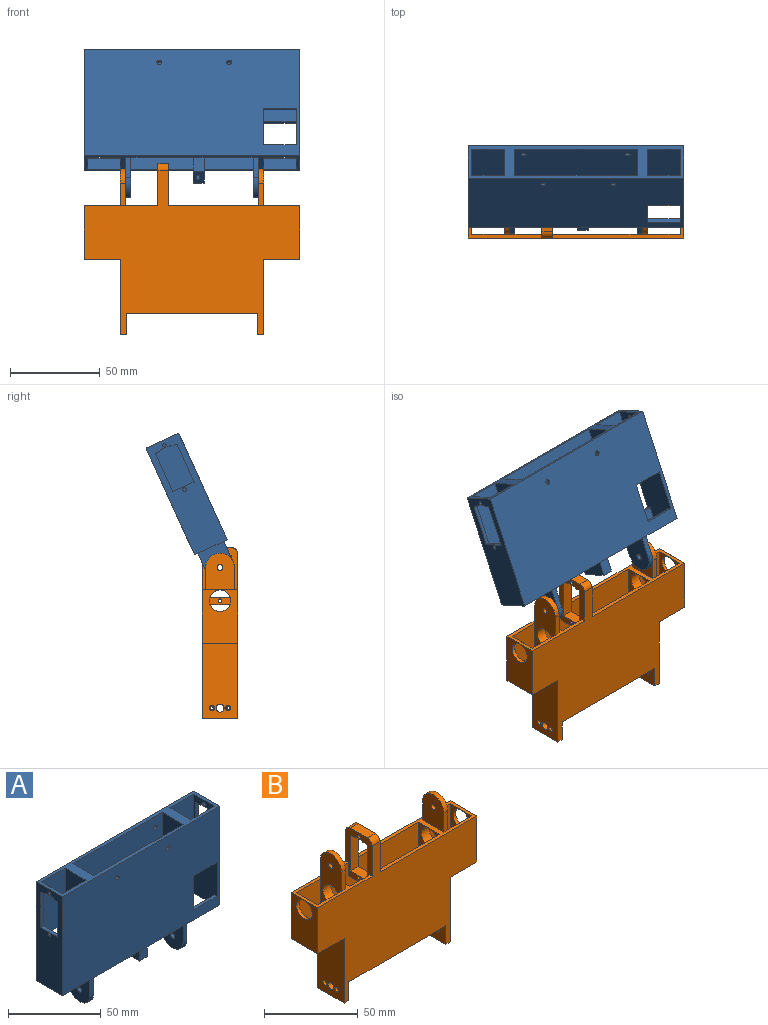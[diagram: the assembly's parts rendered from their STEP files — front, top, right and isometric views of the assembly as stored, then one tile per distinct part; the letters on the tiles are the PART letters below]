
ASSEMBLY  parts=2 mates=1
PART A: 78 faces, bbox 120x20x85.7 mm
  f0: plane 18x6.8mm, normal (0,1,0), area 122.5mm2, adj f17,f24,f33,f75
  f1: plane 18x6.8mm, normal (0,-1,0), area 122.5mm2, adj f17,f24,f33,f73
  f2: plane 18x6.8mm, normal (0,-1,0), area 122.5mm2, adj f27,f30,f33,f71
  f3: plane 120x65.32mm, normal (0,1,0), area 7010.2mm2, adj f16,f17,f21,f24,f27,f30,f32,f33
  f4: plane 13x2mm, normal (0,0,1), area 26mm2, adj f11,f15,f21,f30
  f5: plane 2.8x2mm, normal (0,0,-1), area 5.6mm2, adj f7,f14,f21,f30
  f6: plane 2x0.7mm, normal (0,1,0), area 1.4mm2, adj f8,f13,f21,f30
  f7: plane 2x0.7mm, normal (0,-1,0), area 1.4mm2, adj f5,f8,f21,f30
  f8: plane 6x2mm, normal (0,0,-1), area 12mm2, adj f6,f7,f21,f30
  f9: cylinder r=1mm len=2mm, axis (-1,0,0), area 12.6mm2, adj f21,f30
  f10: cylinder r=1mm len=2mm, axis (-1,0,0), area 12.6mm2, adj f21,f30
  f11: plane 22.8x2mm, normal (0,-1,0), area 45.6mm2, adj f4,f14,f21,f30
  f12: cylinder r=0.7mm len=2mm, axis (-1,0,0), area 2.2mm2, adj f13,f15,f21,f30
  f13: plane 2.8x2mm, normal (0,0,-1), area 5.6mm2, adj f6,f12,f21,f30
  f14: cylinder r=0.7mm len=2mm, axis (1,0,0), area 2.2mm2, adj f5,f11,f21,f30
  f15: plane 22.8x2mm, normal (0,1,0), area 45.6mm2, adj f4,f12,f21,f30
  f16: plane 65.32x20mm, normal (1,0,0), area 990.7mm2, adj f3,f18,f22,f32,f33,f55,f56,f57
  f17: plane 65.32x20mm, normal (-1,0,0), area 818.9mm2, adj f0,f1,f3,f18,f22,f23,f25,f32
  f18: plane 2.8x2mm, normal (0,0,-1), area 5.6mm2, adj f16,f17,f58,f67
  f19: plane 68x65.32mm, normal (0,-1,0), area 4360.7mm2, adj f29,f31,f32,f33,f46,f47,f49,f62
  f20: plane 68x65.32mm, normal (0,1,0), area 4372.6mm2, adj f29,f31,f32,f33,f46,f47,f49,f76
  f21: plane 65.32x20mm, normal (-1,0,0), area 990.7mm2, adj f3,f4,f5,f6,f7,f8,f9,f10
  f22: plane 120x65.32mm, normal (0,-1,0), area 7424.6mm2, adj f16,f17,f21,f24,f32,f33,f74,f75
  f23: plane 36.16x18mm, normal (0,1,0), area 650.9mm2, adj f17,f24,f32,f74
  f24: plane 65.32x20mm, normal (1,0,0), area 1134.6mm2, adj f0,f1,f3,f22,f23,f25,f32,f33
  f25: plane 36.16x18mm, normal (0,-1,0), area 650.9mm2, adj f17,f24,f32,f72
  f26: plane 36.16x18mm, normal (0,-1,0), area 650.9mm2, adj f27,f30,f32,f70
  f27: plane 65.32x18mm, normal (-1,0,0), area 1089.9mm2, adj f2,f3,f26,f28,f32,f33,f70,f71
  f28: plane 65.32x18mm, normal (0,1,0), area 1175.8mm2, adj f27,f30,f32,f33
  f29: plane 85.66x16mm, normal (1,0,0), area 1335.1mm2, adj f19,f20,f32,f37,f41,f42,f43
  f30: plane 65.32x18mm, normal (1,0,0), area 774.1mm2, adj f2,f3,f4,f5,f6,f7,f8,f9
  f31: plane 85.66x16mm, normal (-1,0,0), area 1335.1mm2, adj f19,f20,f32,f36,f38,f39,f40
  f32: plane 120x20mm, normal (0,0,1), area 736mm2, adj f3,f16,f17,f19,f20,f21,f22,f23
  f33: plane 120x20mm, normal (0,0,-1), area 640mm2, adj f0,f1,f2,f3,f16,f17,f19,f20
  f34: plane 20.34x16mm, normal (-1,0,0), area 289.9mm2, adj f33,f37,f41,f42,f43
  f35: plane 20.34x16mm, normal (1,0,0), area 289.9mm2, adj f33,f36,f38,f39,f40
  f36: cylinder r=1.6mm len=3.2mm, axis (1,0,0), area 30.2mm2, adj f31,f35
  f37: cylinder r=1.6mm len=3.2mm, axis (1,0,0), area 30.2mm2, adj f29,f34
  f38: plane 12.34x3mm, normal (0,1,0), area 37mm2, adj f31,f33,f35,f39
  f39: cylinder r=8mm len=16mm, axis (1,0,0), area 75.4mm2, adj f31,f35,f38,f40
  f40: plane 12.34x3mm, normal (0,-1,0), area 37mm2, adj f31,f33,f35,f39
  f41: plane 12.34x3mm, normal (0,-1,0), area 37mm2, adj f29,f33,f34,f42
  f42: cylinder r=8mm len=16mm, axis (1,0,0), area 75.4mm2, adj f29,f34,f41,f43
  f43: plane 12.34x3mm, normal (0,1,0), area 37mm2, adj f29,f33,f34,f42
  f44: plane 8.54x6mm, normal (0,1,0), area 51.2mm2, adj f33,f45,f46,f47
  f45: plane 16x6mm, normal (0,0,-1), area 85.2mm2, adj f44,f46,f47,f48,f50,f51,f52,f53
  f46: plane 18.14x16mm, normal (-1,0,0), area 290.3mm2, adj f19,f20,f44,f45,f48,f49
  f47: plane 18.14x16mm, normal (1,0,0), area 290.3mm2, adj f19,f20,f44,f45,f48,f49
  f48: plane 8.54x6mm, normal (0,-1,0), area 51.2mm2, adj f33,f45,f46,f47
  f49: plane 16x6mm, normal (0,0,1), area 96mm2, adj f19,f20,f46,f47
  f50: plane 12.4x5.69mm, normal (1,0,0), area 59.1mm2, adj f45,f51,f52,f54
  f51: plane 10.21x1.9mm, normal (0,1,-0.06), area 19.4mm2, adj f45,f50,f53,f54
  f52: plane 10.21x1.9mm, normal (0,-1,-0.06), area 19.4mm2, adj f45,f50,f53,f54
  f53: plane 12.4x5.69mm, normal (-1,0,0), area 59.1mm2, adj f45,f51,f52,f54
  f54: cylinder r=2.2mm len=4.4mm, axis (1,0,0), area 13.1mm2, adj f50,f51,f52,f53
  f55: plane 2.8x2mm, normal (0,0,-1), area 5.6mm2, adj f16,f17,f59,f66
  f56: plane 22.8x2mm, normal (0,-1,0), area 45.6mm2, adj f16,f17,f58,f69
  f57: plane 22.8x2mm, normal (0,1,0), area 45.6mm2, adj f16,f17,f59,f69
  f58: cylinder r=0.7mm len=2mm, axis (-1,0,0), area 2.2mm2, adj f16,f17,f18,f56
  f59: cylinder r=0.7mm len=2mm, axis (1,0,0), area 2.2mm2, adj f16,f17,f55,f57
  f60: cylinder r=1mm len=2mm, axis (1,0,0), area 12.6mm2, adj f16,f17
  f61: cylinder r=1mm len=2mm, axis (1,0,0), area 12.6mm2, adj f16,f17
  f62: cylinder r=1.38mm len=2.75mm, axis (0,1,0), area 17.3mm2, adj f3,f19
  f63: cylinder r=1.38mm len=2.75mm, axis (0,1,0), area 17.3mm2, adj f3,f19
  f64: cylinder r=1.38mm len=2.75mm, axis (0,1,0), area 17.3mm2, adj f3,f19
  f65: cylinder r=1.38mm len=2.75mm, axis (0,1,0), area 17.3mm2, adj f3,f19
  f66: plane 2x0.7mm, normal (0,1,0), area 1.4mm2, adj f16,f17,f55,f68
  f67: plane 2x0.7mm, normal (0,-1,0), area 1.4mm2, adj f16,f17,f18,f68
  f68: plane 6x2mm, normal (0,0,-1), area 12mm2, adj f16,f17,f66,f67
  f69: plane 13x2mm, normal (0,0,1), area 26mm2, adj f16,f17,f56,f57
  f70: plane 18x2mm, normal (0,0,-1), area 36mm2, adj f3,f26,f27,f30
  f71: plane 18x2mm, normal (0,0,1), area 36mm2, adj f2,f3,f27,f30
  f72: plane 18x2mm, normal (0,0,-1), area 36mm2, adj f3,f17,f24,f25
  f73: plane 18x2mm, normal (0,0,1), area 36mm2, adj f1,f3,f17,f24
  f74: plane 18x2mm, normal (0,0,-1), area 36mm2, adj f17,f22,f23,f24
  f75: plane 18x2mm, normal (0,0,1), area 36mm2, adj f0,f17,f22,f24
  f76: cylinder r=1.38mm len=2.75mm, axis (0,-1,0), area 17.3mm2, adj f20,f22
  f77: cylinder r=1.38mm len=2.75mm, axis (0,-1,0), area 17.3mm2, adj f20,f22
PART B: 75 faces, bbox 120x20x95.3 mm
  f0: plane 120x91.75mm, normal (0,1,0), area 6190mm2, adj f2,f4,f7,f8,f14,f15,f18,f19
  f1: plane 68x60mm, normal (0,-1,0), area 4016.7mm2, adj f2,f4,f7,f8,f14,f27,f28,f47
  f2: plane 31.8x20mm, normal (1,0,0), area 280.9mm2, adj f0,f1,f3,f5,f6,f7,f9,f47
  f3: plane 6x2.8mm, normal (0,0,-1), area 16.8mm2, adj f2,f4,f51,f67
  f4: plane 31.8x20mm, normal (-1,0,0), area 280.9mm2, adj f0,f1,f3,f5,f6,f8,f9,f47
  f5: plane 120x91.75mm, normal (0,-1,0), area 6202.5mm2, adj f2,f4,f7,f8,f14,f15,f18,f19
  f6: plane 12.83x6mm, normal (0,0,1), area 77mm2, adj f2,f4,f65,f66
  f7: plane 73x20mm, normal (0,0,1), area 372mm2, adj f0,f1,f2,f5,f9,f17,f24,f28
  f8: plane 41x20mm, normal (0,0,1), area 244mm2, adj f0,f1,f4,f5,f9,f16,f20,f27
  f9: plane 68x60mm, normal (0,1,0), area 4029.2mm2, adj f2,f4,f7,f8,f14,f27,f28,f47
  f10: cylinder r=0.8mm len=1.9mm, axis (-1,0,0), area 9.6mm2, adj f55,f64
  f11: cylinder r=0.8mm len=1.9mm, axis (-1,0,0), area 9.6mm2, adj f55,f62
  f12: cylinder r=0.8mm len=1.9mm, axis (-1,0,0), area 9.6mm2, adj f56,f60
  f13: cylinder r=0.8mm len=1.9mm, axis (-1,0,0), area 9.6mm2, adj f56,f58
  f14: plane 73x20mm, normal (0,0,-1), area 372mm2, adj f0,f1,f5,f9,f27,f28,f55,f56
  f15: plane 92.34x20mm, normal (-1,0,0), area 1466.8mm2, adj f0,f5,f21,f22,f25,f32,f34,f36
  f16: plane 20.34x16mm, normal (1,0,0), area 289.9mm2, adj f8,f36,f40,f41,f42
  f17: plane 20.34x16mm, normal (-1,0,0), area 289.9mm2, adj f7,f35,f37,f38,f39
  f18: plane 20x20mm, normal (0,0,-1), area 112mm2, adj f0,f5,f23,f24,f29,f30,f31
  f19: plane 20x3.5mm, normal (0,0,-1), area 70mm2, adj f0,f5,f23,f56
  f20: plane 30x20mm, normal (-1,0,0), area 486.9mm2, adj f0,f5,f8,f21,f45
  f21: plane 20x20mm, normal (0,0,-1), area 112mm2, adj f0,f5,f15,f20,f32,f33,f34
  f22: plane 20x3.5mm, normal (0,0,-1), area 70mm2, adj f0,f5,f15,f55
  f23: plane 92.34x20mm, normal (1,0,0), area 1466.8mm2, adj f0,f5,f18,f19,f26,f29,f31,f35
  f24: plane 30x20mm, normal (1,0,0), area 486.9mm2, adj f0,f5,f7,f18,f43
  f25: cylinder r=2.25mm len=4.5mm, axis (-1,0,0), area 49.5mm2, adj f15,f55
  f26: cylinder r=2.25mm len=4.5mm, axis (-1,0,0), area 49.5mm2, adj f23,f56
  f27: plane 60x16mm, normal (1,0,0), area 846.9mm2, adj f1,f8,f9,f14,f46
  f28: plane 60x16mm, normal (-1,0,0), area 846.9mm2, adj f1,f7,f9,f14,f44
  f29: plane 30x18mm, normal (0,-1,0), area 540mm2, adj f7,f18,f23,f30
  f30: plane 30x16mm, normal (-1,0,0), area 366.9mm2, adj f7,f18,f29,f31,f43
  f31: plane 30x18mm, normal (0,1,0), area 540mm2, adj f7,f18,f23,f30
  f32: plane 30x18mm, normal (0,1,0), area 540mm2, adj f8,f15,f21,f33
  f33: plane 30x16mm, normal (1,0,0), area 366.9mm2, adj f8,f21,f32,f34,f45
  f34: plane 30x18mm, normal (0,-1,0), area 540mm2, adj f8,f15,f21,f33
  f35: cylinder r=1.6mm len=3.2mm, axis (1,0,0), area 30.2mm2, adj f17,f23
  f36: cylinder r=1.6mm len=3.2mm, axis (1,0,0), area 30.2mm2, adj f15,f16
  f37: plane 12.34x3mm, normal (0,-1,0), area 37mm2, adj f7,f17,f23,f39
  f38: plane 12.34x3mm, normal (0,1,0), area 37mm2, adj f7,f17,f23,f39
  f39: cylinder r=8mm len=16mm, axis (1,0,0), area 75.4mm2, adj f17,f23,f37,f38
  f40: cylinder r=8mm len=16mm, axis (1,0,0), area 75.4mm2, adj f15,f16,f41,f42
  f41: plane 12.34x3mm, normal (0,1,0), area 37mm2, adj f8,f15,f16,f40
  f42: plane 12.34x3mm, normal (0,-1,0), area 37mm2, adj f8,f15,f16,f40
  f43: cylinder r=6mm len=12mm, axis (-1,0,0), area 75.4mm2, adj f24,f30
  f44: cylinder r=6mm len=12mm, axis (-1,0,0), area 226.2mm2, adj f23,f28
  f45: cylinder r=6mm len=12mm, axis (1,0,0), area 75.4mm2, adj f20,f33
  f46: cylinder r=6mm len=12mm, axis (1,0,0), area 226.2mm2, adj f15,f27
  f47: plane 16x6mm, normal (0,0,-1), area 96mm2, adj f1,f2,f4,f9
  f48: cylinder r=1mm len=6mm, axis (1,0,0), area 37.7mm2, adj f2,f4
  f49: plane 22.8x6mm, normal (0,-1,0), area 136.8mm2, adj f2,f4,f51,f70
  f50: plane 22.8x6mm, normal (0,1,0), area 136.8mm2, adj f2,f4,f52,f70
  f51: cylinder r=0.7mm len=6mm, axis (-1,0,0), area 6.6mm2, adj f2,f3,f4,f49
  f52: cylinder r=0.7mm len=6mm, axis (1,0,0), area 6.6mm2, adj f2,f4,f50,f53
  f53: plane 6x2.8mm, normal (0,0,-1), area 16.8mm2, adj f2,f4,f52,f68
  f54: cylinder r=1mm len=6mm, axis (1,0,0), area 37.7mm2, adj f2,f4
  f55: plane 20x12mm, normal (1,0,0), area 220.1mm2, adj f0,f5,f10,f11,f14,f22,f25
  f56: plane 20x12mm, normal (-1,0,0), area 220.1mm2, adj f0,f5,f12,f13,f14,f19,f26
  f57: cylinder r=1.5mm len=3mm, axis (1,0,0), area 15.1mm2, adj f23,f58
  f58: plane 3x3mm, normal (1,0,0), area 5.1mm2, adj f13,f57
  f59: cylinder r=1.5mm len=3mm, axis (1,0,0), area 15.1mm2, adj f23,f60
  f60: plane 3x3mm, normal (1,0,0), area 5.1mm2, adj f12,f59
  f61: cylinder r=1.5mm len=3mm, axis (-1,0,0), area 15.1mm2, adj f15,f62
  f62: plane 3x3mm, normal (-1,0,0), area 5.1mm2, adj f11,f61
  f63: cylinder r=1.5mm len=3mm, axis (-1,0,0), area 15.1mm2, adj f15,f64
  f64: plane 3x3mm, normal (-1,0,0), area 5.1mm2, adj f10,f63
  f65: cylinder r=3.58mm len=6mm, axis (-1,0,0), area 33.8mm2, adj f2,f4,f5,f6
  f66: cylinder r=3.58mm len=6mm, axis (-1,0,0), area 33.8mm2, adj f0,f2,f4,f6
  f67: plane 6x0.7mm, normal (0,-1,0), area 4.2mm2, adj f2,f3,f4,f69
  f68: plane 6x0.7mm, normal (0,1,0), area 4.2mm2, adj f2,f4,f53,f69
  f69: plane 6x6mm, normal (0,0,-1), area 36mm2, adj f2,f4,f67,f68
  f70: plane 13x6mm, normal (0,0,1), area 78mm2, adj f2,f4,f49,f50
  f71: cylinder r=1mm len=2mm, axis (0,1,0), area 12.6mm2, adj f0,f1
  f72: cylinder r=1mm len=2mm, axis (0,1,0), area 12.6mm2, adj f0,f1
  f73: cylinder r=1mm len=2mm, axis (0,1,0), area 12.6mm2, adj f0,f1
  f74: cylinder r=1mm len=2mm, axis (0,1,0), area 12.6mm2, adj f0,f1
PLACE A rot(axis=(-1,0,0),24.4deg) t=(1.64,-33.75,33.88)mm
PLACE B t=(1.64,1.15,26.32)mm fixed
MATE revolute B.f35 <-> A.f36  axis (1,0,0) through (-35.36,1.15,110.66)mm
